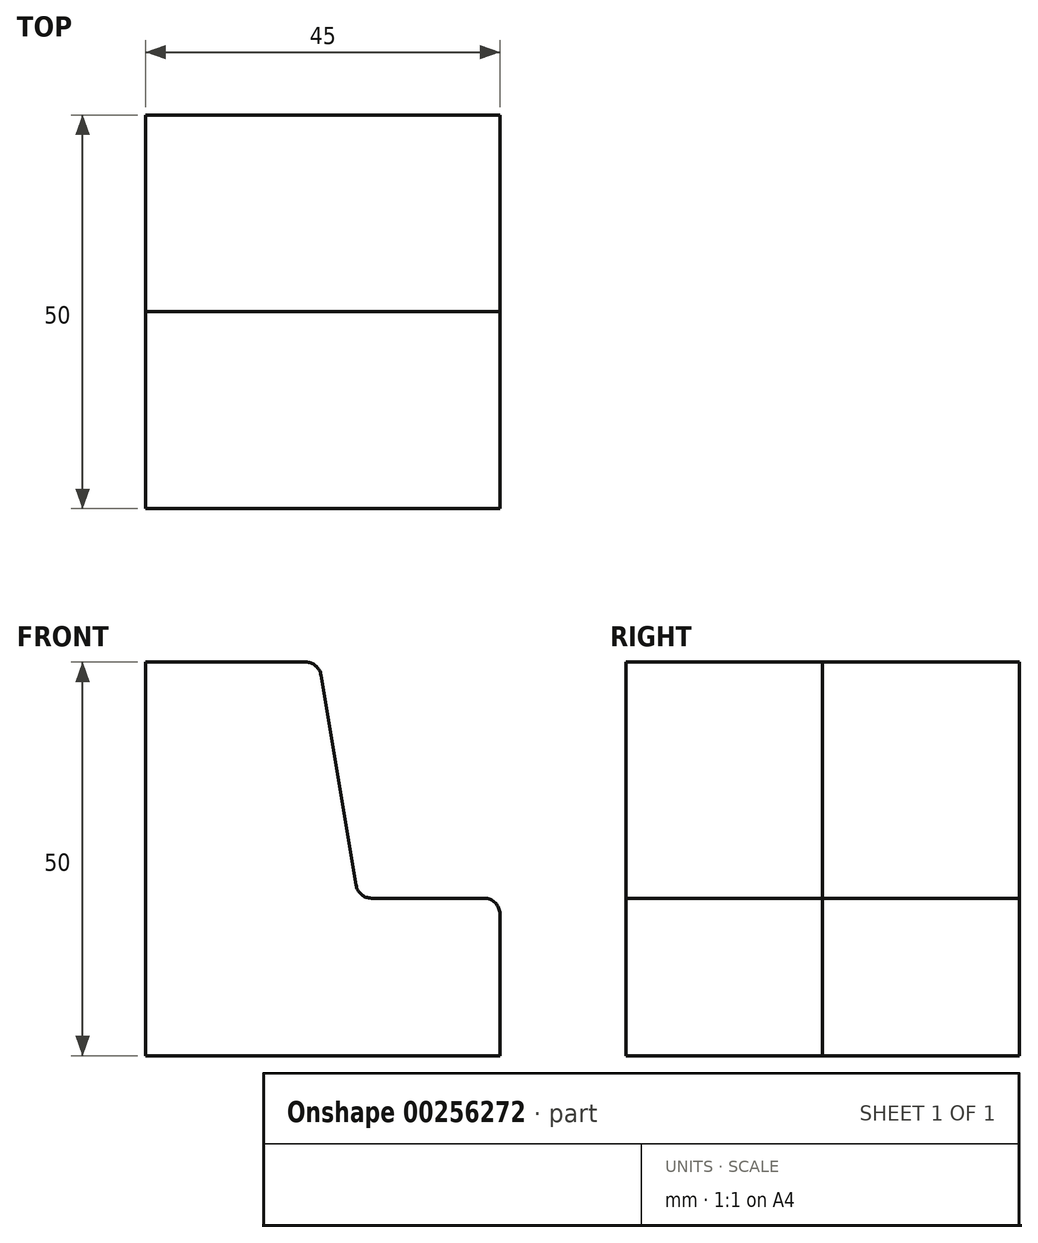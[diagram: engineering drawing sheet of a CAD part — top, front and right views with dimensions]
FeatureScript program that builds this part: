
annotation { "Feature Type Name" : "Feature", "Feature Type Description" : "" }
export const myFeature = defineFeature(function(context is Context, id is Id, definition is map)
    precondition{}
    {
        {
            var Q0;
            Q0=qCreatedBy(makeId("Front.planeOp"),FACE);
            var sketch = newSketch(context, id + "F0", { "sketchPlane" : qUnion([Q0])});
            skLineSegment(sketch, "E0", {"start": v(0, 0) * mm, "end": v(0, 50) * mm});
            skLineSegment(sketch, "E1", {"start": v(0, 50) * mm, "end": v(20.3, 50) * mm});
            skLineSegment(sketch, "E2", {"start": v(22.28, 48.33) * mm, "end": v(26.72, 21.67) * mm});
            skLineSegment(sketch, "E3", {"start": v(28.7, 20) * mm, "end": v(43, 20) * mm});
            skLineSegment(sketch, "E4", {"start": v(45, 18) * mm, "end": v(45, 0) * mm});
            skLineSegment(sketch, "E5", {"start": v(45, 0) * mm, "end": v(0, 0) * mm});
            skPoint(sketch, "E6.visualSharp", {"position": v(22, 50) * mm});
            skArc(sketch, "E6.filletArc", {"start": v(22.28, 48.33) * mm, "mid": v(21.6, 49.53) * mm, "end": v(20.3, 50) * mm});
            skPoint(sketch, "E7.visualSharp", {"position": v(27, 20) * mm});
            skArc(sketch, "E7.filletArc", {"start": v(26.72, 21.67) * mm, "mid": v(27.4, 20.47) * mm, "end": v(28.7, 20) * mm});
            skPoint(sketch, "E8.visualSharp", {"position": v(45, 20) * mm});
            skArc(sketch, "E8.filletArc", {"start": v(45, 18) * mm, "mid": v(44.41, 19.41) * mm, "end": v(43, 20) * mm});
            skLineSegment(sketch, "E9", {"start": v(0, -47.77) * mm, "end": v(0, 67.56) * mm, "construction": true});
            skLineSegment(sketch, "E10", {"start": v(0, 67.56) * mm, "end": v(0, 55.8) * mm, "construction": true});
            skSolve(sketch);
        }
        {
            var Q0;
            Q0=makeQuery(id+"F0.imprint","IMPRINT",FACE,{"disambiguationData":[TD([[makeQuery(id+"F0.imprint","IMPRINT",EDGE,{"derivedFrom":sQuery(id+"F0.wireOp",EDGE,"E0")}),-1.0]])]});
            extrude(context, id + "F1", {"entities" : qUnion([Q0]), "depth" : 25 * mm});
        }
        {
            var Q0;
            Q0=makeQuery(id+"F1.opExtrude","CAP_FACE",FACE,{"disambiguationData":[OSD([sQuery(id+"F0.wireOp",EDGE,"E0"),sQuery(id+"F0.wireOp",EDGE,"E1"),sQuery(id+"F0.wireOp",EDGE,"E2"),sQuery(id+"F0.wireOp",EDGE,"E3"),sQuery(id+"F0.wireOp",EDGE,"E4"),sQuery(id+"F0.wireOp",EDGE,"E5"),sQuery(id+"F0.wireOp",EDGE,"E6.filletArc"),sQuery(id+"F0.wireOp",EDGE,"E7.filletArc"),sQuery(id+"F0.wireOp",EDGE,"E8.filletArc")])],"isStart":false});
            extrude(context, id + "F2", {"entities" : qUnion([Q0]), "depth" : 25 * mm});
        }
    });
